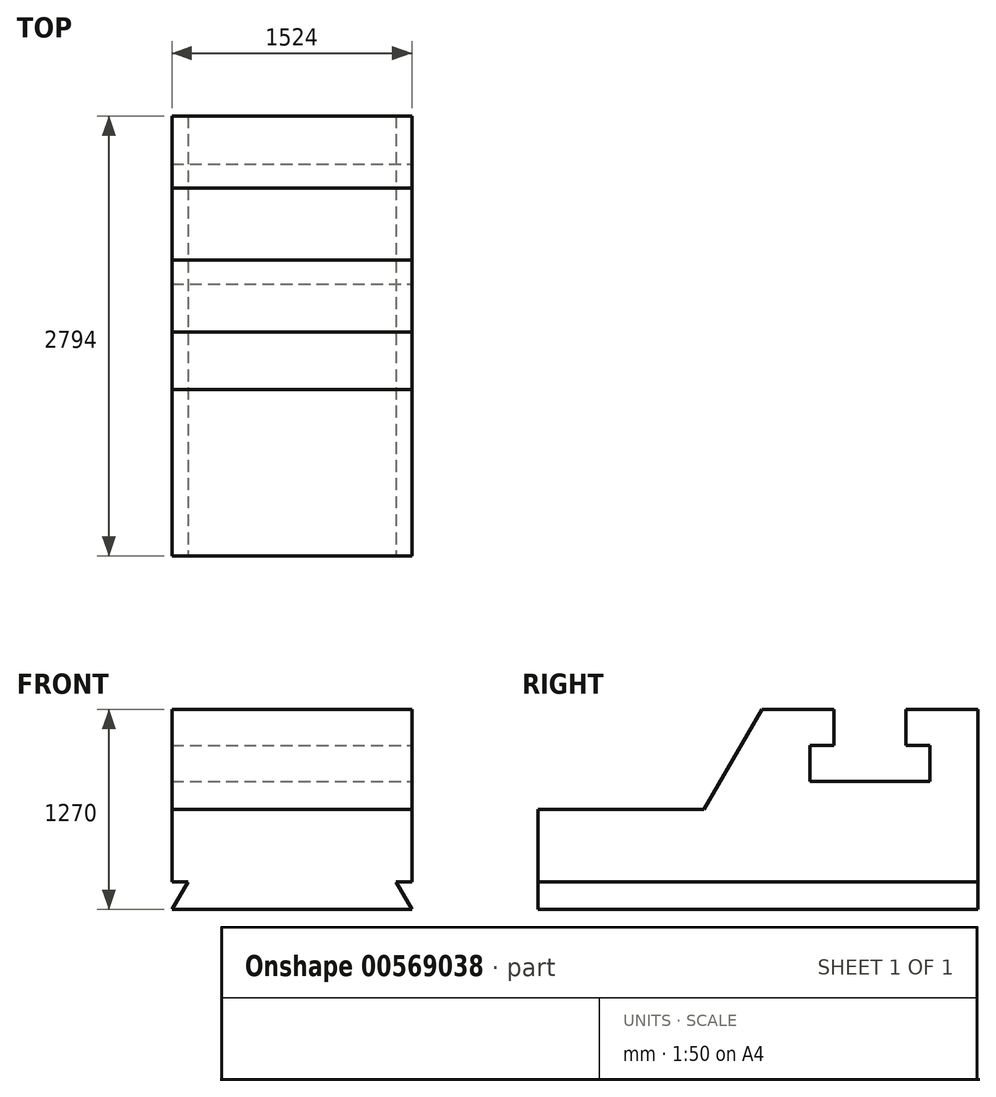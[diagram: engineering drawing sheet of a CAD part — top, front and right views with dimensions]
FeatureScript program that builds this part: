
annotation { "Feature Type Name" : "Feature", "Feature Type Description" : "" }
export const myFeature = defineFeature(function(context is Context, id is Id, definition is map)
    precondition{}
    {
        {
            var Q0;
            Q0=qCreatedBy(makeId("Right.planeOp"),FACE);
            var sketch = newSketch(context, id + "F0", { "sketchPlane" : qUnion([Q0])});
            skLineSegment(sketch, "E0", {"start": v(36.08, -62.08) * mm, "end": v(2830.08, -62.08) * mm});
            skLineSegment(sketch, "E1", {"start": v(2830.08, -62.08) * mm, "end": v(2830.08, 1207.92) * mm});
            skLineSegment(sketch, "E2", {"start": v(36.08, -62.08) * mm, "end": v(36.08, 572.92) * mm});
            skLineSegment(sketch, "E3", {"start": v(36.08, 572.92) * mm, "end": v(1091.86, 572.92) * mm});
            skLineSegment(sketch, "E4", {"start": v(2830.08, 1207.92) * mm, "end": v(2372.88, 1207.92) * mm});
            skLineSegment(sketch, "E5", {"start": v(2372.88, 1207.92) * mm, "end": v(2372.88, 979.32) * mm});
            skLineSegment(sketch, "E6", {"start": v(2372.88, 979.32) * mm, "end": v(2525.28, 979.32) * mm});
            skLineSegment(sketch, "E7", {"start": v(2525.28, 979.32) * mm, "end": v(2525.28, 750.72) * mm});
            skLineSegment(sketch, "E8", {"start": v(2525.28, 750.72) * mm, "end": v(1763.28, 750.72) * mm});
            skLineSegment(sketch, "E9", {"start": v(1763.28, 750.72) * mm, "end": v(1763.28, 979.32) * mm});
            skLineSegment(sketch, "E10", {"start": v(1763.28, 979.32) * mm, "end": v(1915.68, 979.32) * mm});
            skLineSegment(sketch, "E11", {"start": v(1915.68, 979.32) * mm, "end": v(1915.68, 1207.92) * mm});
            skLineSegment(sketch, "E12", {"start": v(1915.68, 1207.92) * mm, "end": v(1458.48, 1207.92) * mm});
            skLineSegment(sketch, "E13", {"start": v(1458.48, 1207.92) * mm, "end": v(1091.86, 572.92) * mm});
            skSolve(sketch);
        }
        {
            var Q0;
            Q0=makeQuery(id+"F0.imprint","IMPRINT",FACE,{"disambiguationData":[TD([[makeQuery(id+"F0.imprint","IMPRINT",EDGE,{"derivedFrom":sQuery(id+"F0.wireOp",EDGE,"E0")}),1.0]])]});
            extrude(context, id + "F1", {"entities" : qUnion([Q0]), "oppositeDirection" : true, "depth" : 1524 * mm, "offsetDistance" : 25.4 * mm});
        }
        {
            var Q0;
            Q0=makeQuery(id+"F1.opExtrude","SWEPT_FACE",FACE,{"disambiguationData":[OSD([sQuery(id+"F0.wireOp",EDGE,"E2")])]});
            var sketch = newSketch(context, id + "F2", { "sketchPlane" : qUnion([Q0])});
            skLineSegment(sketch, "E14", {"start": v(-1524, -62.08) * mm, "end": v(-1422.4, 113.9) * mm});
            skLineSegment(sketch, "E15", {"start": v(-1422.4, 113.9) * mm, "end": v(-1524, 113.9) * mm});
            skLineSegment(sketch, "E16", {"start": v(0, -62.08) * mm, "end": v(-101.6, 113.9) * mm});
            skLineSegment(sketch, "E17", {"start": v(-101.6, 113.9) * mm, "end": v(0, 113.9) * mm});
            skSolve(sketch);
        }
        {
            var Q0;
            {var subQ0=sQuery(id+"F2.wireOp",EDGE,"E14");Q0=makeQuery(id+"F2.imprint","IMPRINT",FACE,{"disambiguationData":[TD([[makeQuery(id+"F2.imprint","IMPRINT",EDGE,{"derivedFrom":subQ0}),1.0]])]});}
            var Q1;
            {var subQ0=sQuery(id+"F2.wireOp",EDGE,"E16");Q1=makeQuery(id+"F2.imprint","IMPRINT",FACE,{"disambiguationData":[TD([[makeQuery(id+"F2.imprint","IMPRINT",EDGE,{"derivedFrom":subQ0}),-1.0]])]});}
            extrude(context, id + "F3", {"entities" : qUnion([Q0, Q1]), "operationType" : NewBodyOperationType.REMOVE, "oppositeDirection" : true, "depth" : 2794 * mm, "offsetDistance" : 25.4 * mm});
        }
    });
